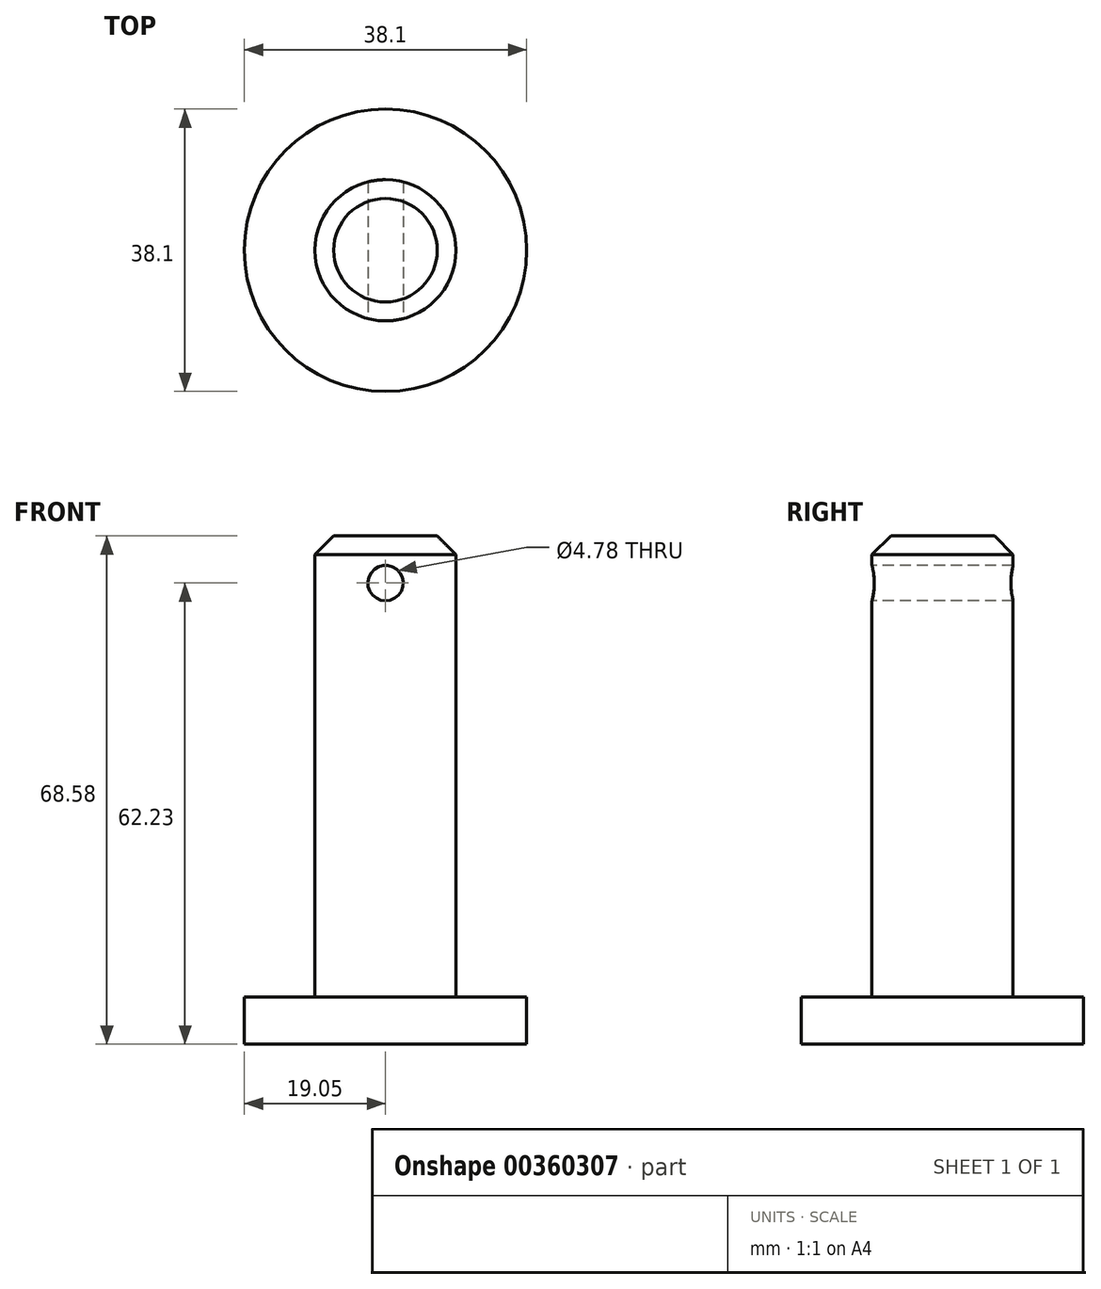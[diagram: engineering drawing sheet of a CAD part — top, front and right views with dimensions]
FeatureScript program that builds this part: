
annotation { "Feature Type Name" : "Feature", "Feature Type Description" : "" }
export const myFeature = defineFeature(function(context is Context, id is Id, definition is map)
    precondition{}
    {
        {
            var Q0;
            Q0=qCreatedBy(makeId("Top.planeOp"),FACE);
            var sketch = newSketch(context, id + "F0", { "sketchPlane" : qUnion([Q0])});
            skCircle(sketch, "E0", {"center": v(0, 0) * mm, "radius": 19.05 * mm});
            skSolve(sketch);
        }
        {
            var Q0;
            Q0 = qSketchRegion(id + "F0", true);
            extrude(context, id + "F1", {"entities" : qUnion([Q0]), "depth" : 6.35 * mm});
        }
        {
            var Q0;
            Q0=makeQuery(id+"F1.opExtrude","CAP_FACE",FACE,{"disambiguationData":[OSD([sQuery(id+"F0.wireOp",EDGE,"E0")])],"isStart":false});
            var sketch = newSketch(context, id + "F2", { "sketchPlane" : qUnion([Q0])});
            skCircle(sketch, "E1", {"center": v(0, 0) * mm, "radius": 9.53 * mm});
            skSolve(sketch);
        }
        {
            var Q0;
            Q0=makeQuery(id+"F2.imprint","IMPRINT",FACE,{"disambiguationData":[TD([[makeQuery(id+"F2.imprint","IMPRINT",EDGE,{"derivedFrom":sQuery(id+"F2.wireOp",EDGE,"E1")}),1.0]])]});
            extrude(context, id + "F3", {"entities" : qUnion([Q0]), "operationType" : NewBodyOperationType.ADD, "depth" : 62.23 * mm});
        }
        {
            var Q0;
            Q0=makeQuery(id+"F3.opExtrude","CAP_EDGE",EDGE,{"disambiguationData":[OSD([sQuery(id+"F2.wireOp",EDGE,"E1")])],"isStart":false});
            chamfer(context, id + "F4", {"entities" : qUnion([Q0]), "width" : 2.54 * mm, "tangentPropagation" : true});
        }
        {
            var Q0;
            Q0=qCreatedBy(makeId("Front.planeOp"),FACE);
            var sketch = newSketch(context, id + "F5", { "sketchPlane" : qUnion([Q0])});
            skPoint(sketch, "E2", {"position": v(0, 62.23) * mm});
            skCircle(sketch, "E3", {"center": v(0, 62.23) * mm, "radius": 2.39 * mm});
            skSolve(sketch);
        }
        {
            var Q0;
            Q0=makeQuery(id+"F5.imprint","IMPRINT",FACE,{"disambiguationData":[TD([[makeQuery(id+"F5.imprint","IMPRINT",EDGE,{"derivedFrom":sQuery(id+"F5.wireOp",EDGE,"E3")}),1.0]])]});
            extrude(context, id + "F6", {"entities" : qUnion([Q0]), "operationType" : NewBodyOperationType.REMOVE, "endBound" : BoundingType.SYMMETRIC, "oppositeDirection" : true, "depth" : 25.4 * mm});
        }
    });
